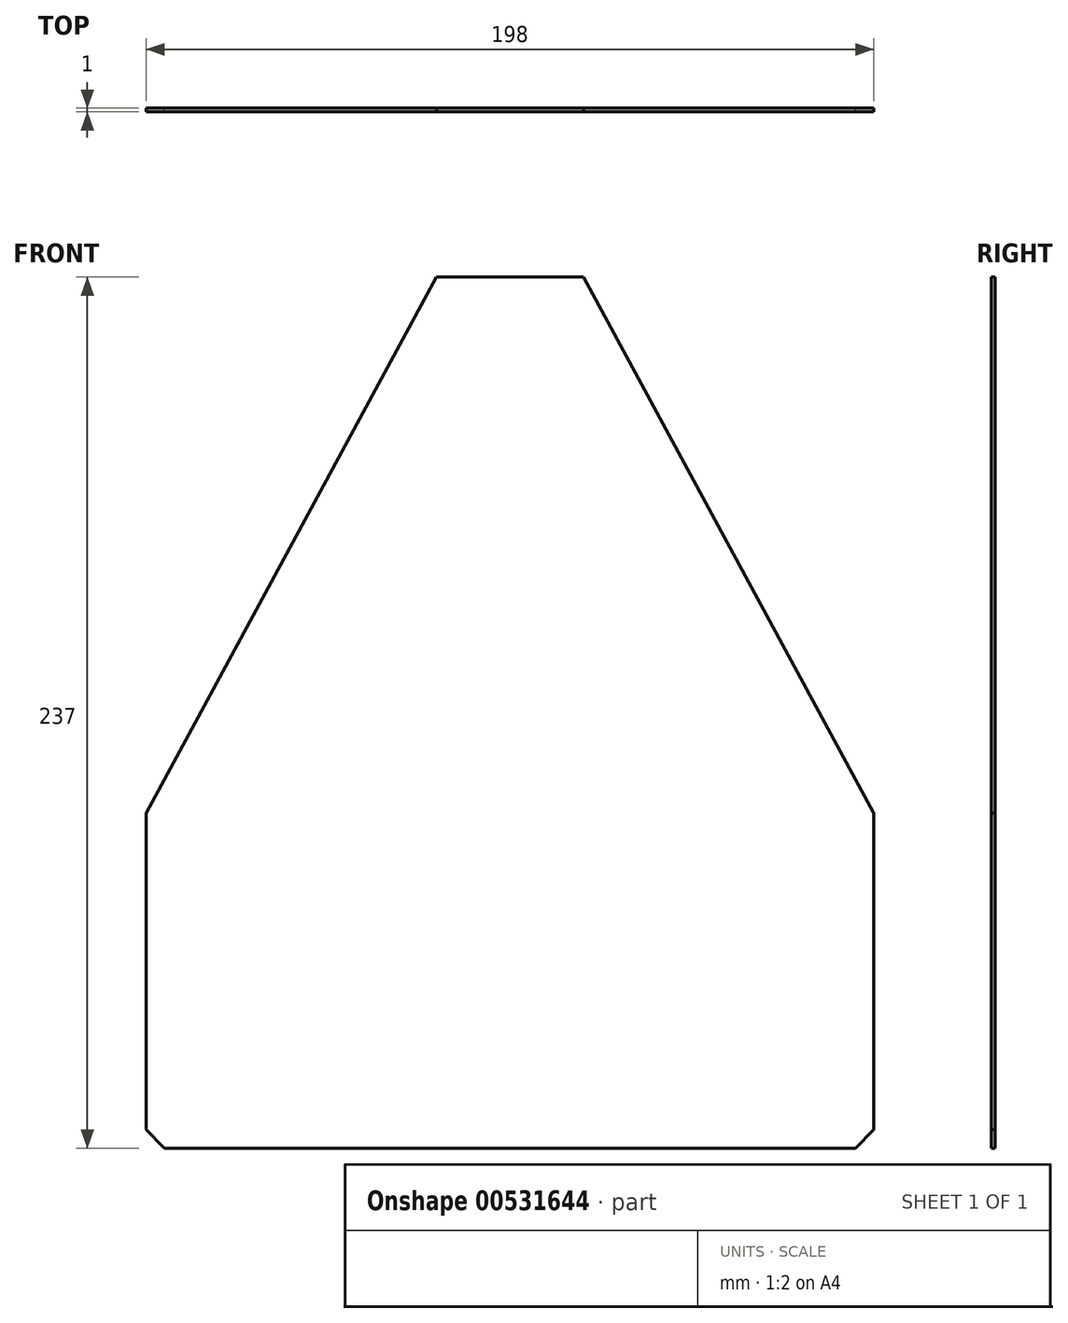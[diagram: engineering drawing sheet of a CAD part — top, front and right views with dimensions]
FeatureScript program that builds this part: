
annotation { "Feature Type Name" : "Feature", "Feature Type Description" : "" }
export const myFeature = defineFeature(function(context is Context, id is Id, definition is map)
    precondition{}
    {
        {
            var Q0;
            Q0=qCreatedBy(makeId("Front.planeOp"),FACE);
            var sketch = newSketch(context, id + "F0", { "sketchPlane" : qUnion([Q0])});
            skLineSegment(sketch, "E0.bottom", {"start": v(-94, -102) * mm, "end": v(94, -102) * mm});
            skLineSegment(sketch, "E0.top", {"start": v(-20.21, 135) * mm, "end": v(20, 135) * mm});
            skLineSegment(sketch, "E0.left", {"start": v(-99, -97) * mm, "end": v(-99, -10.92) * mm});
            skLineSegment(sketch, "E0.right", {"start": v(99, -97) * mm, "end": v(99, -10.92) * mm});
            skLineSegment(sketch, "E1", {"start": v(0, -79.7) * mm, "end": v(0, -102) * mm});
            skLineSegment(sketch, "E2", {"start": v(-99, -97) * mm, "end": v(-94, -102) * mm});
            skLineSegment(sketch, "E3", {"start": v(94, -102) * mm, "end": v(99, -97) * mm});
            skPoint(sketch, "E4.orphan", {"position": v(-99, -102) * mm});
            skPoint(sketch, "E5.right.end.orphan", {"position": v(-94, -97) * mm});
            skPoint(sketch, "E6.MirrorCS.end.orphan", {"position": v(94, -97) * mm});
            skPoint(sketch, "E7.orphan", {"position": v(99, -102) * mm});
            skLineSegment(sketch, "E8", {"start": v(94, -102) * mm, "end": v(94, -97) * mm});
            skPoint(sketch, "E9", {"position": v(-20.21, 135) * mm});
            skPoint(sketch, "E10", {"position": v(20, 135) * mm});
            skPoint(sketch, "E11", {"position": v(-14, 135) * mm});
            skPoint(sketch, "E12", {"position": v(14, 135) * mm});
            skLineSegment(sketch, "E13", {"start": v(14, 135) * mm, "end": v(99, -22) * mm});
            skLineSegment(sketch, "E14", {"start": v(14, 135) * mm, "end": v(20, 135) * mm});
            skPoint(sketch, "E15", {"position": v(101.14, -14.86) * mm});
            skLineSegment(sketch, "E16", {"start": v(20, 135) * mm, "end": v(99, -10.92) * mm});
            skPoint(sketch, "E17", {"position": v(99, -10.92) * mm});
            skLineSegment(sketch, "E18.MirrorCS", {"start": v(-14, 135) * mm, "end": v(-99, -22) * mm});
            skLineSegment(sketch, "E19.MirrorCS", {"start": v(-20, 135) * mm, "end": v(-99, -10.92) * mm});
            skSolve(sketch);
        }
        {
            var Q0;
            {var subQ0=sQuery(id+"F0.wireOp",EDGE,"E18.MirrorCS");Q0=makeQuery(id+"F0.imprint","IMPRINT",FACE,{"disambiguationData":[TD([[makeQuery(id+"F0.imprint","IMPRINT",EDGE,{"derivedFrom":subQ0}),-1.0]])]});}
            var Q1;
            {var subQ0=sQuery(id+"F0.wireOp",EDGE,"E2");Q1=makeQuery(id+"F0.imprint","IMPRINT",FACE,{"disambiguationData":[TD([[makeQuery(id+"F0.imprint","IMPRINT",EDGE,{"derivedFrom":subQ0}),1.0]])]});}
            var Q2;
            {var subQ2=sQuery(id+"F0.wireOp",EDGE,"E13");Q2=makeQuery(id+"F0.imprint","IMPRINT",FACE,{"disambiguationData":[TD([[makeQuery(id+"F0.imprint","IMPRINT",EDGE,{"derivedFrom":subQ2}),1.0]])]});}
            extrude(context, id + "F1", {"entities" : qUnion([Q0, Q1, Q2]), "depth" : 1 * mm, "offsetDistance" : 25 * mm});
        }
    });
